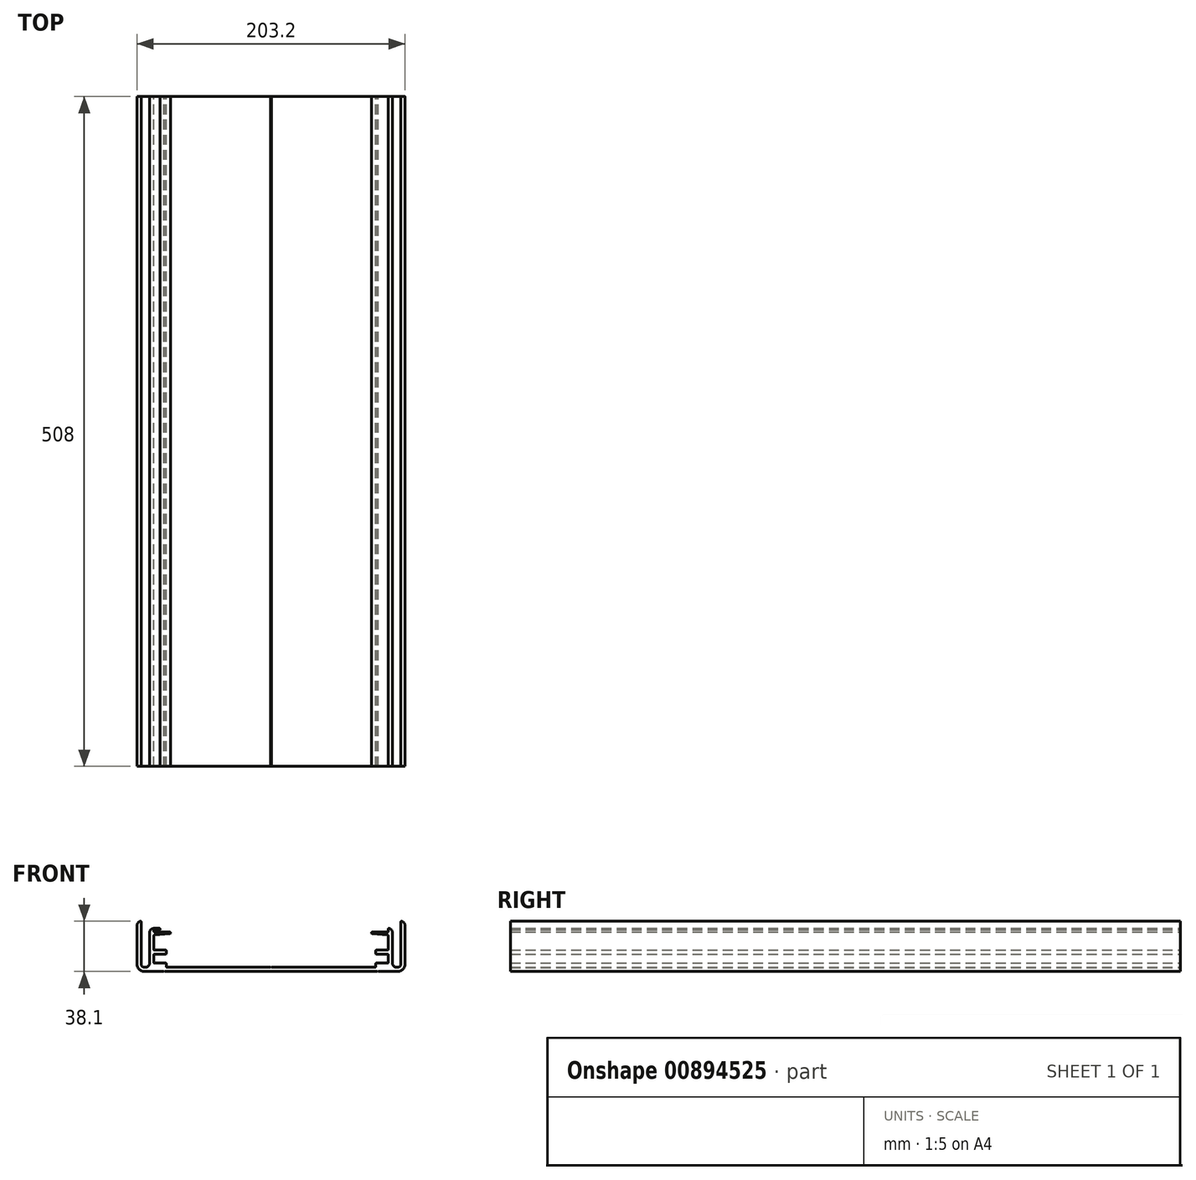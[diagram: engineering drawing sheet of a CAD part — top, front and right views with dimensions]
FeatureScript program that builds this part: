
annotation { "Feature Type Name" : "Feature", "Feature Type Description" : "" }
export const myFeature = defineFeature(function(context is Context, id is Id, definition is map)
    precondition{}
    {
        {
            var Q0;
            Q0=qCreatedBy(makeId("Front.planeOp"),FACE);
            var sketch = newSketch(context, id + "F0", { "sketchPlane" : qUnion([Q0])});
            skLineSegment(sketch, "E0", {"start": v(-109.94, 32.02) * mm, "end": v(-93.65, 25.02) * mm});
            skLineSegment(sketch, "E1", {"start": v(-93.65, 25.02) * mm, "end": v(-89.08, 25.02) * mm});
            skLineSegment(sketch, "E2", {"start": v(-106.68, 29.78) * mm, "end": v(-106.07, 31.2) * mm});
            skLineSegment(sketch, "E3", {"start": v(-106.07, 31.2) * mm, "end": v(-109.94, 32.02) * mm});
            skLineSegment(sketch, "E4", {"start": v(-109.94, 32.02) * mm, "end": v(-106.68, 29.78) * mm});
            skLineSegment(sketch, "E5", {"start": v(-110.7, 32.42) * mm, "end": v(-110.33, 32.8) * mm});
            skLineSegment(sketch, "E6", {"start": v(-109.95, 32.42) * mm, "end": v(-110.33, 32.8) * mm});
            skLineSegment(sketch, "E7", {"start": v(51.95, 32.42) * mm, "end": v(51.57, 32.8) * mm});
            skLineSegment(sketch, "E8", {"start": v(51.19, 32.42) * mm, "end": v(51.57, 32.8) * mm});
            skLineSegment(sketch, "E9", {"start": v(-113.5, 66.15) * mm, "end": v(-113.5, 74.73) * mm});
            skArc(sketch, "E10", {"start": v(49.62, 35.6) * mm, "mid": v(49.88, 35.7) * mm, "end": v(50, 35.97) * mm});
            skArc(sketch, "E11", {"start": v(-108.75, 35.97) * mm, "mid": v(-108.64, 35.7) * mm, "end": v(-108.37, 35.6) * mm});
            skLineSegment(sketch, "E12", {"start": v(-108.37, 35.6) * mm, "end": v(-29.63, 35.6) * mm});
            skLineSegment(sketch, "E13", {"start": v(-29.12, 35.6) * mm, "end": v(49.62, 35.6) * mm});
            skLineSegment(sketch, "E14", {"start": v(51.95, 26.45) * mm, "end": v(51.73, 26.65) * mm});
            skLineSegment(sketch, "E15", {"start": v(51.73, 26.65) * mm, "end": v(50.6, 26.65) * mm});
            skLineSegment(sketch, "E16", {"start": v(50.6, 26.65) * mm, "end": v(50.36, 26.45) * mm});
            skLineSegment(sketch, "E17", {"start": v(50.36, 26.45) * mm, "end": v(50.36, 24.54) * mm});
            skLineSegment(sketch, "E18", {"start": v(51.27, 27.09) * mm, "end": v(51.27, 23.9) * mm});
            skLineSegment(sketch, "E19", {"start": v(51.27, 23.9) * mm, "end": v(52.63, 23.9) * mm});
            skLineSegment(sketch, "E20", {"start": v(50.36, 24.54) * mm, "end": v(50.6, 24.33) * mm});
            skLineSegment(sketch, "E21", {"start": v(50.6, 24.33) * mm, "end": v(51.73, 24.33) * mm});
            skLineSegment(sketch, "E22", {"start": v(51.73, 24.33) * mm, "end": v(51.95, 24.54) * mm});
            skLineSegment(sketch, "E23", {"start": v(-109.74, 14.45) * mm, "end": v(-109.97, 14.65) * mm});
            skLineSegment(sketch, "E24", {"start": v(-109.97, 14.65) * mm, "end": v(-111.1, 14.65) * mm});
            skLineSegment(sketch, "E25", {"start": v(-111.1, 14.65) * mm, "end": v(-111.33, 14.45) * mm});
            skLineSegment(sketch, "E26", {"start": v(-111.33, 14.45) * mm, "end": v(-111.33, 12.54) * mm});
            skLineSegment(sketch, "E27", {"start": v(-110.42, 15.09) * mm, "end": v(-110.42, 11.9) * mm});
            skLineSegment(sketch, "E28", {"start": v(-110.42, 11.9) * mm, "end": v(-109.07, 11.9) * mm});
            skLineSegment(sketch, "E29", {"start": v(-111.33, 12.54) * mm, "end": v(-111.1, 12.33) * mm});
            skLineSegment(sketch, "E30", {"start": v(-111.1, 12.33) * mm, "end": v(-109.97, 12.33) * mm});
            skLineSegment(sketch, "E31", {"start": v(-109.97, 12.33) * mm, "end": v(-109.74, 12.54) * mm});
            skLineSegment(sketch, "E32", {"start": v(51.95, 32.42) * mm, "end": v(66.68, 32.42) * mm});
            skLineSegment(sketch, "E33", {"start": v(-109.95, 32.42) * mm, "end": v(51.19, 32.42) * mm});
            skLineSegment(sketch, "E34", {"start": v(-118.28, 31.04) * mm, "end": v(-118.28, 16.63) * mm});
            skArc(sketch, "E35", {"start": v(-108.75, 38.39) * mm, "mid": v(-108.87, 38.66) * mm, "end": v(-109.13, 38.77) * mm});
            skLineSegment(sketch, "E36", {"start": v(-125.44, 32.42) * mm, "end": v(-110.7, 32.42) * mm});
            skLineSegment(sketch, "E37", {"start": v(-110.33, 35.85) * mm, "end": v(-110.33, 11.74) * mm});
            skLineSegment(sketch, "E38", {"start": v(92.16, -20.96) * mm, "end": v(91.21, -19.68) * mm});
            skLineSegment(sketch, "E39", {"start": v(91.21, -17.46) * mm, "end": v(92.16, -16.19) * mm});
            skLineSegment(sketch, "E40", {"start": v(93.8, -20.16) * mm, "end": v(94.65, -18.04) * mm});
            skLineSegment(sketch, "E41", {"start": v(94.65, -18.04) * mm, "end": v(95.5, -20.16) * mm});
            skLineSegment(sketch, "E42", {"start": v(95.5, -20.16) * mm, "end": v(93.8, -20.16) * mm});
            skLineSegment(sketch, "E43", {"start": v(97.56, -20.96) * mm, "end": v(98.51, -19.68) * mm});
            skLineSegment(sketch, "E44", {"start": v(98.51, -19.68) * mm, "end": v(98.51, -17.46) * mm});
            skLineSegment(sketch, "E45", {"start": v(98.51, -17.46) * mm, "end": v(97.56, -16.19) * mm});
            skLineSegment(sketch, "E46", {"start": v(101.07, -20.16) * mm, "end": v(101.29, -20.16) * mm});
            skLineSegment(sketch, "E47", {"start": v(101.29, -20.16) * mm, "end": v(101.29, -19.95) * mm});
            skLineSegment(sketch, "E48", {"start": v(101.29, -19.95) * mm, "end": v(101.07, -19.95) * mm});
            skLineSegment(sketch, "E49", {"start": v(101.07, -19.95) * mm, "end": v(101.07, -20.16) * mm});
            skLineSegment(sketch, "E50", {"start": v(105.6, -17.84) * mm, "end": v(105.6, -19.32) * mm});
            skLineSegment(sketch, "E51", {"start": v(105.6, -19.32) * mm, "end": v(104.92, -20.16) * mm});
            skLineSegment(sketch, "E52", {"start": v(104.92, -20.16) * mm, "end": v(104.01, -20.16) * mm});
            skLineSegment(sketch, "E53", {"start": v(104.01, -20.16) * mm, "end": v(103.33, -19.32) * mm});
            skLineSegment(sketch, "E54", {"start": v(103.33, -19.32) * mm, "end": v(103.33, -17.84) * mm});
            skLineSegment(sketch, "E55", {"start": v(103.33, -17.84) * mm, "end": v(104.01, -16.98) * mm});
            skLineSegment(sketch, "E56", {"start": v(104.01, -16.98) * mm, "end": v(104.92, -16.98) * mm});
            skLineSegment(sketch, "E57", {"start": v(104.92, -16.98) * mm, "end": v(105.6, -17.84) * mm});
            skLineSegment(sketch, "E58", {"start": v(108.77, -18.25) * mm, "end": v(108.1, -18.89) * mm});
            skLineSegment(sketch, "E59", {"start": v(108.77, -20.16) * mm, "end": v(106.5, -20.16) * mm});
            skLineSegment(sketch, "E60", {"start": v(106.5, -20.16) * mm, "end": v(106.5, -19.74) * mm});
            skLineSegment(sketch, "E61", {"start": v(106.5, -19.74) * mm, "end": v(107.19, -19.1) * mm});
            skLineSegment(sketch, "E62", {"start": v(107.19, -19.1) * mm, "end": v(108.1, -18.89) * mm});
            skLineSegment(sketch, "E63", {"start": v(106.5, -17.62) * mm, "end": v(107.19, -16.98) * mm});
            skLineSegment(sketch, "E64", {"start": v(107.19, -16.98) * mm, "end": v(108.1, -16.98) * mm});
            skLineSegment(sketch, "E65", {"start": v(108.1, -16.98) * mm, "end": v(108.77, -17.62) * mm});
            skLineSegment(sketch, "E66", {"start": v(108.77, -17.62) * mm, "end": v(108.77, -18.25) * mm});
            skLineSegment(sketch, "E67", {"start": v(111.5, -18.47) * mm, "end": v(111.95, -18.89) * mm});
            skLineSegment(sketch, "E68", {"start": v(110.6, -18.47) * mm, "end": v(111.5, -18.47) * mm});
            skLineSegment(sketch, "E69", {"start": v(111.5, -18.47) * mm, "end": v(111.95, -18.04) * mm});
            skLineSegment(sketch, "E70", {"start": v(111.95, -18.89) * mm, "end": v(111.95, -19.74) * mm});
            skLineSegment(sketch, "E71", {"start": v(111.95, -19.74) * mm, "end": v(111.5, -20.16) * mm});
            skLineSegment(sketch, "E72", {"start": v(111.5, -20.16) * mm, "end": v(109.9, -20.16) * mm});
            skLineSegment(sketch, "E73", {"start": v(109.9, -20.16) * mm, "end": v(109.68, -19.95) * mm});
            skLineSegment(sketch, "E74", {"start": v(109.9, -17.2) * mm, "end": v(110.14, -16.98) * mm});
            skLineSegment(sketch, "E75", {"start": v(110.14, -16.98) * mm, "end": v(111.5, -16.98) * mm});
            skLineSegment(sketch, "E76", {"start": v(111.5, -16.98) * mm, "end": v(111.95, -17.42) * mm});
            skLineSegment(sketch, "E77", {"start": v(111.95, -17.42) * mm, "end": v(111.95, -18.04) * mm});
            skLineSegment(sketch, "E78", {"start": v(118.3, -18.25) * mm, "end": v(117.85, -18.68) * mm});
            skLineSegment(sketch, "E79", {"start": v(117.85, -18.68) * mm, "end": v(116.03, -18.68) * mm});
            skLineSegment(sketch, "E80", {"start": v(116.03, -20.16) * mm, "end": v(116.03, -16.98) * mm});
            skLineSegment(sketch, "E81", {"start": v(116.03, -16.98) * mm, "end": v(117.85, -16.98) * mm});
            skLineSegment(sketch, "E82", {"start": v(117.85, -16.98) * mm, "end": v(118.3, -17.42) * mm});
            skLineSegment(sketch, "E83", {"start": v(118.3, -17.42) * mm, "end": v(118.3, -18.25) * mm});
            skLineSegment(sketch, "E84", {"start": v(117.4, -18.68) * mm, "end": v(118.3, -20.16) * mm});
            skLineSegment(sketch, "E85", {"start": v(120.12, -20.16) * mm, "end": v(120.34, -20.16) * mm});
            skLineSegment(sketch, "E86", {"start": v(120.34, -20.16) * mm, "end": v(120.34, -19.95) * mm});
            skLineSegment(sketch, "E87", {"start": v(120.34, -19.95) * mm, "end": v(120.12, -19.95) * mm});
            skLineSegment(sketch, "E88", {"start": v(120.12, -19.95) * mm, "end": v(120.12, -20.16) * mm});
            skLineSegment(sketch, "E89", {"start": v(123.91, -20.96) * mm, "end": v(122.96, -19.68) * mm});
            skLineSegment(sketch, "E90", {"start": v(122.96, -19.68) * mm, "end": v(122.96, -17.46) * mm});
            skLineSegment(sketch, "E91", {"start": v(122.96, -17.46) * mm, "end": v(123.91, -16.19) * mm});
            skLineSegment(sketch, "E92", {"start": v(126.24, -20.16) * mm, "end": v(127.15, -20.16) * mm});
            skLineSegment(sketch, "E93", {"start": v(126.24, -17.42) * mm, "end": v(126.69, -16.98) * mm});
            skLineSegment(sketch, "E94", {"start": v(129.41, -20.16) * mm, "end": v(130.32, -20.16) * mm});
            skLineSegment(sketch, "E95", {"start": v(129.41, -17.42) * mm, "end": v(129.86, -16.98) * mm});
            skLineSegment(sketch, "E96", {"start": v(129.86, -16.98) * mm, "end": v(129.86, -20.16) * mm});
            skLineSegment(sketch, "E97", {"start": v(132.49, -20.96) * mm, "end": v(133.44, -19.68) * mm});
            skLineSegment(sketch, "E98", {"start": v(133.44, -19.68) * mm, "end": v(133.44, -17.46) * mm});
            skLineSegment(sketch, "E99", {"start": v(133.44, -17.46) * mm, "end": v(132.49, -16.19) * mm});
            skLineSegment(sketch, "E100", {"start": v(66.98, 70.95) * mm, "end": v(67.65, 72.64) * mm});
            skLineSegment(sketch, "E101", {"start": v(67.65, 72.64) * mm, "end": v(68.33, 70.95) * mm});
            skLineSegment(sketch, "E102", {"start": v(68.33, 70.95) * mm, "end": v(66.98, 70.95) * mm});
            skLineSegment(sketch, "E103", {"start": v(-127, 70.86) * mm, "end": v(-126.33, 72.55) * mm});
            skLineSegment(sketch, "E104", {"start": v(-126.33, 72.55) * mm, "end": v(-125.65, 70.86) * mm});
            skLineSegment(sketch, "E105", {"start": v(-125.65, 70.86) * mm, "end": v(-127, 70.86) * mm});
            skLineSegment(sketch, "E106", {"start": v(-118.28, 37.9) * mm, "end": v(-118.28, 33.4) * mm});
            skArc(sketch, "E107", {"start": v(-128.52, 70.5) * mm, "mid": v(-130.29, 69.39) * mm, "end": v(-130.98, 67.41) * mm});
            skArc(sketch, "E108", {"start": v(-127.8, 69.93) * mm, "mid": v(-128.02, 70.4) * mm, "end": v(-128.52, 70.5) * mm});
            skArc(sketch, "E109", {"start": v(-127.8, 37.96) * mm, "mid": v(-127.11, 36.29) * mm, "end": v(-125.44, 35.6) * mm});
            skArc(sketch, "E110", {"start": v(-130.98, 37.96) * mm, "mid": v(-129.36, 34.04) * mm, "end": v(-125.44, 32.42) * mm});
            skArc(sketch, "E111", {"start": v(-124.63, 35.6) * mm, "mid": v(-122.38, 36.52) * mm, "end": v(-121.45, 38.77) * mm});
            skLineSegment(sketch, "E112", {"start": v(-125.44, 35.6) * mm, "end": v(-124.63, 35.6) * mm});
            skLineSegment(sketch, "E113", {"start": v(-130.98, 37.96) * mm, "end": v(-130.98, 67.41) * mm});
            skLineSegment(sketch, "E114", {"start": v(-127.8, 37.96) * mm, "end": v(-127.8, 69.93) * mm});
            skLineSegment(sketch, "E115", {"start": v(-108.75, 38.39) * mm, "end": v(-108.75, 35.97) * mm});
            skArc(sketch, "E116", {"start": v(72.22, 67.41) * mm, "mid": v(71.53, 69.39) * mm, "end": v(69.76, 70.5) * mm});
            skArc(sketch, "E117", {"start": v(50.38, 38.77) * mm, "mid": v(50.1, 38.66) * mm, "end": v(50, 38.39) * mm});
            skArc(sketch, "E118", {"start": v(59.14, 38.77) * mm, "mid": v(59.4, 38.88) * mm, "end": v(59.52, 39.15) * mm});
            skArc(sketch, "E119", {"start": v(62.7, 38.77) * mm, "mid": v(63.63, 36.52) * mm, "end": v(65.87, 35.6) * mm});
            skArc(sketch, "E120", {"start": v(66.68, 35.6) * mm, "mid": v(68.35, 36.29) * mm, "end": v(69.05, 37.96) * mm});
            skArc(sketch, "E121", {"start": v(66.68, 32.42) * mm, "mid": v(70.6, 34.04) * mm, "end": v(72.22, 37.96) * mm});
            skLineSegment(sketch, "E122", {"start": v(65.87, 35.6) * mm, "end": v(66.68, 35.6) * mm});
            skArc(sketch, "E123", {"start": v(69.76, 70.5) * mm, "mid": v(69.27, 70.4) * mm, "end": v(69.05, 69.93) * mm});
            skLineSegment(sketch, "E124", {"start": v(50, 35.97) * mm, "end": v(50, 38.39) * mm});
            skLineSegment(sketch, "E125", {"start": v(50.38, 38.77) * mm, "end": v(59.14, 38.77) * mm});
            skLineSegment(sketch, "E126", {"start": v(72.22, 37.96) * mm, "end": v(72.22, 67.41) * mm});
            skLineSegment(sketch, "E127", {"start": v(69.05, 37.96) * mm, "end": v(69.05, 69.93) * mm});
            skLineSegment(sketch, "E128", {"start": v(-29.63, 35.6) * mm, "end": v(-29.38, 35.34) * mm});
            skLineSegment(sketch, "E129", {"start": v(-29.12, 35.6) * mm, "end": v(-29.38, 35.34) * mm});
            skLineSegment(sketch, "E130", {"start": v(-30.82, 45.5) * mm, "end": v(-30.82, 44.28) * mm});
            skLineSegment(sketch, "E131", {"start": v(-30.82, 44.28) * mm, "end": v(-29.97, 43.42) * mm});
            skLineSegment(sketch, "E132", {"start": v(-29.97, 43.42) * mm, "end": v(-28.75, 43.42) * mm});
            skLineSegment(sketch, "E133", {"start": v(-28.75, 43.42) * mm, "end": v(-27.88, 44.28) * mm});
            skLineSegment(sketch, "E134", {"start": v(-27.88, 44.28) * mm, "end": v(-27.88, 45.5) * mm});
            skLineSegment(sketch, "E135", {"start": v(-27.88, 45.5) * mm, "end": v(-28.75, 46.36) * mm});
            skLineSegment(sketch, "E136", {"start": v(-28.75, 46.36) * mm, "end": v(-29.97, 46.36) * mm});
            skLineSegment(sketch, "E137", {"start": v(-29.97, 46.36) * mm, "end": v(-30.82, 45.5) * mm});
            skLineSegment(sketch, "E138", {"start": v(-31.55, 45.8) * mm, "end": v(-31.55, 43.97) * mm});
            skLineSegment(sketch, "E139", {"start": v(-31.55, 43.97) * mm, "end": v(-30.26, 42.68) * mm});
            skLineSegment(sketch, "E140", {"start": v(-30.26, 42.68) * mm, "end": v(-28.44, 42.68) * mm});
            skLineSegment(sketch, "E141", {"start": v(-28.44, 42.68) * mm, "end": v(-27.16, 43.97) * mm});
            skLineSegment(sketch, "E142", {"start": v(-27.16, 43.97) * mm, "end": v(-27.16, 45.8) * mm});
            skLineSegment(sketch, "E143", {"start": v(-27.16, 45.8) * mm, "end": v(-28.44, 47.1) * mm});
            skLineSegment(sketch, "E144", {"start": v(-28.44, 47.1) * mm, "end": v(-30.26, 47.1) * mm});
            skLineSegment(sketch, "E145", {"start": v(-30.26, 47.1) * mm, "end": v(-31.55, 45.8) * mm});
            skLineSegment(sketch, "E146", {"start": v(-28.86, 40.34) * mm, "end": v(-29.9, 40.34) * mm});
            skLineSegment(sketch, "E147", {"start": v(-113.25, 63.86) * mm, "end": v(-106.42, 63.86) * mm});
            skLineSegment(sketch, "E148", {"start": v(-105.58, 75.44) * mm, "end": v(-105.58, 86.36) * mm});
            skLineSegment(sketch, "E149", {"start": v(-105.58, 62.26) * mm, "end": v(-105.58, 72.73) * mm});
            skLineSegment(sketch, "E150", {"start": v(57.68, 65.46) * mm, "end": v(58.36, 67.15) * mm});
            skLineSegment(sketch, "E151", {"start": v(58.36, 67.15) * mm, "end": v(59.03, 65.46) * mm});
            skLineSegment(sketch, "E152", {"start": v(59.03, 65.46) * mm, "end": v(57.68, 65.46) * mm});
            skLineSegment(sketch, "E153", {"start": v(45, 62.94) * mm, "end": v(45.68, 64.64) * mm});
            skLineSegment(sketch, "E154", {"start": v(45.68, 64.64) * mm, "end": v(46.35, 62.94) * mm});
            skLineSegment(sketch, "E155", {"start": v(46.35, 62.94) * mm, "end": v(45, 62.94) * mm});
            skLineSegment(sketch, "E156", {"start": v(47.9, 48.79) * mm, "end": v(48.57, 50.48) * mm});
            skLineSegment(sketch, "E157", {"start": v(48.57, 50.48) * mm, "end": v(49.24, 48.79) * mm});
            skLineSegment(sketch, "E158", {"start": v(49.24, 48.79) * mm, "end": v(47.9, 48.79) * mm});
            skLineSegment(sketch, "E159", {"start": v(48.08, 43.57) * mm, "end": v(48.75, 45.26) * mm});
            skLineSegment(sketch, "E160", {"start": v(48.75, 45.26) * mm, "end": v(49.43, 43.57) * mm});
            skLineSegment(sketch, "E161", {"start": v(49.43, 43.57) * mm, "end": v(48.08, 43.57) * mm});
            skLineSegment(sketch, "E162", {"start": v(57.3, 57.72) * mm, "end": v(57.98, 59.42) * mm});
            skLineSegment(sketch, "E163", {"start": v(57.98, 59.42) * mm, "end": v(58.66, 57.72) * mm});
            skLineSegment(sketch, "E164", {"start": v(58.66, 57.72) * mm, "end": v(57.3, 57.72) * mm});
            skLineSegment(sketch, "E165", {"start": v(-117.42, 57.63) * mm, "end": v(-116.75, 59.32) * mm});
            skLineSegment(sketch, "E166", {"start": v(-116.75, 59.32) * mm, "end": v(-116.07, 57.63) * mm});
            skLineSegment(sketch, "E167", {"start": v(-116.07, 57.63) * mm, "end": v(-117.42, 57.63) * mm});
            skLineSegment(sketch, "E168", {"start": v(-108.2, 49.35) * mm, "end": v(-107.52, 51.04) * mm});
            skLineSegment(sketch, "E169", {"start": v(-107.52, 51.04) * mm, "end": v(-106.84, 49.35) * mm});
            skLineSegment(sketch, "E170", {"start": v(-106.84, 49.35) * mm, "end": v(-108.2, 49.35) * mm});
            skLineSegment(sketch, "E171", {"start": v(-107.91, 43) * mm, "end": v(-107.24, 44.7) * mm});
            skLineSegment(sketch, "E172", {"start": v(-107.24, 44.7) * mm, "end": v(-106.56, 43) * mm});
            skLineSegment(sketch, "E173", {"start": v(-106.56, 43) * mm, "end": v(-107.91, 43) * mm});
            skLineSegment(sketch, "E174", {"start": v(-105.21, 59.96) * mm, "end": v(-104.54, 61.65) * mm});
            skLineSegment(sketch, "E175", {"start": v(-104.54, 61.65) * mm, "end": v(-103.86, 59.96) * mm});
            skLineSegment(sketch, "E176", {"start": v(-103.86, 59.96) * mm, "end": v(-105.21, 59.96) * mm});
            skArc(sketch, "E177", {"start": v(150.69, 128.9) * mm, "mid": v(149.97, 128.6) * mm, "end": v(149.67, 127.89) * mm});
            skArc(sketch, "E178", {"start": v(149.67, 113.41) * mm, "mid": v(149.97, 112.7) * mm, "end": v(150.69, 112.4) * mm});
            skArc(sketch, "E179", {"start": v(203.26, 112.4) * mm, "mid": v(203.98, 112.7) * mm, "end": v(204.28, 113.41) * mm});
            skArc(sketch, "E180", {"start": v(204.28, 127.89) * mm, "mid": v(203.98, 128.6) * mm, "end": v(203.26, 128.9) * mm});
            skArc(sketch, "E181", {"start": v(122.43, -114.05) * mm, "mid": v(122.52, -114.16) * mm, "end": v(122.66, -114.2) * mm});
            skArc(sketch, "E182", {"start": v(122.3, -112.39) * mm, "mid": v(122.12, -112.47) * mm, "end": v(122.06, -112.67) * mm});
            skArc(sketch, "E183", {"start": v(122.06, -110.84) * mm, "mid": v(122.12, -111.04) * mm, "end": v(122.3, -111.12) * mm});
            skArc(sketch, "E184", {"start": v(122.66, -109.31) * mm, "mid": v(122.52, -109.35) * mm, "end": v(122.43, -109.46) * mm});
            skArc(sketch, "E185", {"start": v(122.06, -112.67) * mm, "mid": v(122.2, -113.37) * mm, "end": v(122.43, -114.05) * mm});
            skArc(sketch, "E186", {"start": v(121.33, -114.7) * mm, "mid": v(121.8, -115.26) * mm, "end": v(122.5, -115.47) * mm});
            skArc(sketch, "E187", {"start": v(122.5, -108.04) * mm, "mid": v(121.8, -108.25) * mm, "end": v(121.33, -108.8) * mm});
            skArc(sketch, "E188", {"start": v(122.43, -109.46) * mm, "mid": v(122.2, -110.14) * mm, "end": v(122.06, -110.84) * mm});
            skArc(sketch, "E189", {"start": v(121.33, -108.8) * mm, "mid": v(120.72, -111.76) * mm, "end": v(121.33, -114.7) * mm});
            skArc(sketch, "E190", {"start": v(142.26, -114.2) * mm, "mid": v(142.4, -114.15) * mm, "end": v(142.5, -114.04) * mm});
            skArc(sketch, "E191", {"start": v(141.11, -114.04) * mm, "mid": v(141.2, -114.15) * mm, "end": v(141.34, -114.2) * mm});
            skArc(sketch, "E192", {"start": v(142.5, -110.96) * mm, "mid": v(142.4, -110.84) * mm, "end": v(142.26, -110.8) * mm});
            skArc(sketch, "E193", {"start": v(141.34, -110.8) * mm, "mid": v(141.2, -110.84) * mm, "end": v(141.11, -110.96) * mm});
            skArc(sketch, "E194", {"start": v(141.11, -110.96) * mm, "mid": v(140.85, -112.5) * mm, "end": v(141.11, -114.04) * mm});
            skArc(sketch, "E195", {"start": v(142.5, -114.04) * mm, "mid": v(142.75, -112.5) * mm, "end": v(142.5, -110.96) * mm});
            skArc(sketch, "E196", {"start": v(137.15, -114.04) * mm, "mid": v(137.24, -114.15) * mm, "end": v(137.38, -114.2) * mm});
            skArc(sketch, "E197", {"start": v(137.38, -110.8) * mm, "mid": v(137.24, -110.84) * mm, "end": v(137.15, -110.96) * mm});
            skArc(sketch, "E198", {"start": v(136.03, -114.66) * mm, "mid": v(136.5, -115.25) * mm, "end": v(137.21, -115.47) * mm});
            skArc(sketch, "E199", {"start": v(137.21, -109.52) * mm, "mid": v(136.5, -109.75) * mm, "end": v(136.03, -110.33) * mm});
            skArc(sketch, "E200", {"start": v(140, -114.66) * mm, "mid": v(140.46, -115.25) * mm, "end": v(141.17, -115.47) * mm});
            skArc(sketch, "E201", {"start": v(142.43, -115.47) * mm, "mid": v(143.15, -115.25) * mm, "end": v(143.61, -114.66) * mm});
            skArc(sketch, "E202", {"start": v(143.61, -110.33) * mm, "mid": v(143.15, -109.75) * mm, "end": v(142.43, -109.52) * mm});
            skArc(sketch, "E203", {"start": v(141.17, -109.52) * mm, "mid": v(140.46, -109.75) * mm, "end": v(140, -110.33) * mm});
            skArc(sketch, "E204", {"start": v(143.61, -114.66) * mm, "mid": v(144.02, -112.5) * mm, "end": v(143.61, -110.33) * mm});
            skArc(sketch, "E205", {"start": v(137.15, -110.96) * mm, "mid": v(136.89, -112.5) * mm, "end": v(137.15, -114.04) * mm});
            skArc(sketch, "E206", {"start": v(136.03, -110.33) * mm, "mid": v(135.62, -112.5) * mm, "end": v(136.03, -114.66) * mm});
            skArc(sketch, "E207", {"start": v(140, -110.33) * mm, "mid": v(139.58, -112.5) * mm, "end": v(140, -114.66) * mm});
            skArc(sketch, "E208", {"start": v(125.23, -115.47) * mm, "mid": v(125.4, -115.4) * mm, "end": v(125.48, -115.22) * mm});
            skArc(sketch, "E209", {"start": v(125.48, -114.45) * mm, "mid": v(125.4, -114.27) * mm, "end": v(125.23, -114.2) * mm});
            skArc(sketch, "E210", {"start": v(125.23, -112.39) * mm, "mid": v(125.4, -112.32) * mm, "end": v(125.48, -112.14) * mm});
            skArc(sketch, "E211", {"start": v(125.48, -111.37) * mm, "mid": v(125.4, -111.2) * mm, "end": v(125.23, -111.12) * mm});
            skArc(sketch, "E212", {"start": v(125.48, -108.29) * mm, "mid": v(125.4, -108.11) * mm, "end": v(125.23, -108.04) * mm});
            skArc(sketch, "E213", {"start": v(125.23, -109.31) * mm, "mid": v(125.4, -109.24) * mm, "end": v(125.48, -109.07) * mm});
            skArc(sketch, "E214", {"start": v(139.02, -115.47) * mm, "mid": v(139.2, -115.4) * mm, "end": v(139.27, -115.22) * mm});
            skArc(sketch, "E215", {"start": v(139.27, -114.45) * mm, "mid": v(139.2, -114.27) * mm, "end": v(139.02, -114.2) * mm});
            skArc(sketch, "E216", {"start": v(139.02, -110.8) * mm, "mid": v(139.2, -110.72) * mm, "end": v(139.27, -110.55) * mm});
            skArc(sketch, "E217", {"start": v(139.27, -109.77) * mm, "mid": v(139.2, -109.6) * mm, "end": v(139.02, -109.52) * mm});
            skArc(sketch, "E218", {"start": v(149.93, -109.51) * mm, "mid": v(149.84, -109.37) * mm, "end": v(149.68, -109.31) * mm});
            skArc(sketch, "E219", {"start": v(149.14, -109.31) * mm, "mid": v(148.98, -109.37) * mm, "end": v(148.9, -109.51) * mm});
            skArc(sketch, "E220", {"start": v(150.11, -112.22) * mm, "mid": v(150.3, -112.13) * mm, "end": v(150.35, -111.93) * mm});
            skArc(sketch, "E221", {"start": v(148.47, -111.93) * mm, "mid": v(148.52, -112.13) * mm, "end": v(148.71, -112.22) * mm});
            skArc(sketch, "E222", {"start": v(151.97, -115.47) * mm, "mid": v(152.16, -115.38) * mm, "end": v(152.21, -115.18) * mm});
            skArc(sketch, "E223", {"start": v(150.94, -115.27) * mm, "mid": v(151.02, -115.41) * mm, "end": v(151.18, -115.47) * mm});
            skArc(sketch, "E224", {"start": v(150.66, -113.7) * mm, "mid": v(150.58, -113.54) * mm, "end": v(150.42, -113.49) * mm});
            skArc(sketch, "E225", {"start": v(148.4, -113.49) * mm, "mid": v(148.24, -113.54) * mm, "end": v(148.16, -113.7) * mm});
            skArc(sketch, "E226", {"start": v(147.64, -115.47) * mm, "mid": v(147.8, -115.41) * mm, "end": v(147.88, -115.27) * mm});
            skArc(sketch, "E227", {"start": v(146.6, -115.18) * mm, "mid": v(146.66, -115.38) * mm, "end": v(146.85, -115.47) * mm});
            skArc(sketch, "E228", {"start": v(151, -108.25) * mm, "mid": v(150.9, -108.1) * mm, "end": v(150.75, -108.04) * mm});
            skArc(sketch, "E229", {"start": v(148.07, -108.04) * mm, "mid": v(147.92, -108.1) * mm, "end": v(147.83, -108.25) * mm});
            skArc(sketch, "E230", {"start": v(154, -108.29) * mm, "mid": v(153.94, -108.11) * mm, "end": v(153.76, -108.04) * mm});
            skArc(sketch, "E231", {"start": v(152.99, -108.04) * mm, "mid": v(152.81, -108.11) * mm, "end": v(152.74, -108.29) * mm});
            skArc(sketch, "E232", {"start": v(153.76, -115.47) * mm, "mid": v(153.94, -115.4) * mm, "end": v(154, -115.22) * mm});
            skArc(sketch, "E233", {"start": v(152.74, -115.22) * mm, "mid": v(152.81, -115.4) * mm, "end": v(152.99, -115.47) * mm});
            skArc(sketch, "E234", {"start": v(157.65, -115.15) * mm, "mid": v(157.53, -114.94) * mm, "end": v(157.28, -114.94) * mm});
            skArc(sketch, "E235", {"start": v(158.68, -115.47) * mm, "mid": v(158.85, -115.4) * mm, "end": v(158.92, -115.22) * mm});
            skArc(sketch, "E236", {"start": v(157.65, -115.22) * mm, "mid": v(157.72, -115.4) * mm, "end": v(157.9, -115.47) * mm});
            skArc(sketch, "E237", {"start": v(154.73, -109.52) * mm, "mid": v(154.56, -109.6) * mm, "end": v(154.48, -109.77) * mm});
            skArc(sketch, "E238", {"start": v(155.75, -109.77) * mm, "mid": v(155.68, -109.6) * mm, "end": v(155.5, -109.52) * mm});
            skArc(sketch, "E239", {"start": v(158.92, -109.77) * mm, "mid": v(158.85, -109.6) * mm, "end": v(158.68, -109.52) * mm});
            skArc(sketch, "E240", {"start": v(157.9, -109.52) * mm, "mid": v(157.72, -109.6) * mm, "end": v(157.65, -109.77) * mm});
            skArc(sketch, "E241", {"start": v(168.5, -108.68) * mm, "mid": v(168.68, -108.6) * mm, "end": v(168.75, -108.43) * mm});
            skArc(sketch, "E242", {"start": v(168.75, -108.29) * mm, "mid": v(168.68, -108.11) * mm, "end": v(168.5, -108.04) * mm});
            skArc(sketch, "E243", {"start": v(167.48, -108.43) * mm, "mid": v(167.55, -108.6) * mm, "end": v(167.73, -108.68) * mm});
            skArc(sketch, "E244", {"start": v(168.75, -109.77) * mm, "mid": v(168.68, -109.6) * mm, "end": v(168.5, -109.52) * mm});
            skArc(sketch, "E245", {"start": v(167.73, -109.52) * mm, "mid": v(167.55, -109.6) * mm, "end": v(167.48, -109.77) * mm});
            skArc(sketch, "E246", {"start": v(168.5, -115.47) * mm, "mid": v(168.68, -115.4) * mm, "end": v(168.75, -115.22) * mm});
            skArc(sketch, "E247", {"start": v(167.48, -115.22) * mm, "mid": v(167.55, -115.4) * mm, "end": v(167.73, -115.47) * mm});
            skArc(sketch, "E248", {"start": v(166.76, -115.47) * mm, "mid": v(166.93, -115.4) * mm, "end": v(167, -115.22) * mm});
            skArc(sketch, "E249", {"start": v(165.74, -115.22) * mm, "mid": v(165.8, -115.4) * mm, "end": v(165.98, -115.47) * mm});
            skArc(sketch, "E250", {"start": v(163.59, -115.47) * mm, "mid": v(163.76, -115.4) * mm, "end": v(163.83, -115.22) * mm});
            skArc(sketch, "E251", {"start": v(162.57, -115.22) * mm, "mid": v(162.64, -115.4) * mm, "end": v(162.81, -115.47) * mm});
            skArc(sketch, "E252", {"start": v(160.42, -115.47) * mm, "mid": v(160.6, -115.4) * mm, "end": v(160.66, -115.22) * mm});
            skArc(sketch, "E253", {"start": v(159.4, -115.22) * mm, "mid": v(159.47, -115.4) * mm, "end": v(159.64, -115.47) * mm});
            skArc(sketch, "E254", {"start": v(163.57, -110.16) * mm, "mid": v(163.71, -110.26) * mm, "end": v(163.89, -110.23) * mm});
            skArc(sketch, "E255", {"start": v(160.66, -109.84) * mm, "mid": v(160.79, -110.05) * mm, "end": v(161.03, -110.05) * mm});
            skArc(sketch, "E256", {"start": v(160.66, -109.77) * mm, "mid": v(160.6, -109.6) * mm, "end": v(160.42, -109.52) * mm});
            skArc(sketch, "E257", {"start": v(159.64, -109.52) * mm, "mid": v(159.47, -109.6) * mm, "end": v(159.4, -109.77) * mm});
            skArc(sketch, "E258", {"start": v(167.73, -108.04) * mm, "mid": v(167.55, -108.11) * mm, "end": v(167.48, -108.29) * mm});
            skArc(sketch, "E259", {"start": v(170.25, -115.47) * mm, "mid": v(170.42, -115.4) * mm, "end": v(170.5, -115.22) * mm});
            skArc(sketch, "E260", {"start": v(169.22, -115.22) * mm, "mid": v(169.3, -115.4) * mm, "end": v(169.47, -115.47) * mm});
            skArc(sketch, "E261", {"start": v(169.47, -109.52) * mm, "mid": v(169.3, -109.6) * mm, "end": v(169.22, -109.77) * mm});
            skArc(sketch, "E262", {"start": v(170.5, -109.84) * mm, "mid": v(170.61, -110.05) * mm, "end": v(170.86, -110.05) * mm});
            skArc(sketch, "E263", {"start": v(170.5, -109.77) * mm, "mid": v(170.42, -109.6) * mm, "end": v(170.25, -109.52) * mm});
            skArc(sketch, "E264", {"start": v(173.42, -115.47) * mm, "mid": v(173.59, -115.4) * mm, "end": v(173.66, -115.22) * mm});
            skArc(sketch, "E265", {"start": v(172.4, -115.22) * mm, "mid": v(172.47, -115.4) * mm, "end": v(172.64, -115.47) * mm});
            skArc(sketch, "E266", {"start": v(178.33, -115.47) * mm, "mid": v(178.5, -115.4) * mm, "end": v(178.57, -115.22) * mm});
            skArc(sketch, "E267", {"start": v(177.3, -115.22) * mm, "mid": v(177.38, -115.4) * mm, "end": v(177.55, -115.47) * mm});
            skArc(sketch, "E268", {"start": v(177.3, -115.15) * mm, "mid": v(177.18, -114.94) * mm, "end": v(176.94, -114.94) * mm});
            skArc(sketch, "E269", {"start": v(178.57, -109.77) * mm, "mid": v(178.5, -109.6) * mm, "end": v(178.33, -109.52) * mm});
            skArc(sketch, "E270", {"start": v(177.55, -109.52) * mm, "mid": v(177.38, -109.6) * mm, "end": v(177.3, -109.77) * mm});
            skArc(sketch, "E271", {"start": v(175.4, -109.77) * mm, "mid": v(175.33, -109.6) * mm, "end": v(175.16, -109.52) * mm});
            skArc(sketch, "E272", {"start": v(174.38, -109.52) * mm, "mid": v(174.2, -109.6) * mm, "end": v(174.14, -109.77) * mm});
            skArc(sketch, "E273", {"start": v(183.22, -110.16) * mm, "mid": v(183.37, -110.26) * mm, "end": v(183.54, -110.23) * mm});
            skArc(sketch, "E274", {"start": v(180.32, -109.84) * mm, "mid": v(180.44, -110.05) * mm, "end": v(180.69, -110.05) * mm});
            skArc(sketch, "E275", {"start": v(180.32, -109.77) * mm, "mid": v(180.25, -109.6) * mm, "end": v(180.07, -109.52) * mm});
            skArc(sketch, "E276", {"start": v(179.3, -109.52) * mm, "mid": v(179.12, -109.6) * mm, "end": v(179.05, -109.77) * mm});
            skArc(sketch, "E277", {"start": v(186.41, -115.47) * mm, "mid": v(186.59, -115.4) * mm, "end": v(186.66, -115.22) * mm});
            skArc(sketch, "E278", {"start": v(183.24, -115.47) * mm, "mid": v(183.42, -115.4) * mm, "end": v(183.49, -115.22) * mm});
            skArc(sketch, "E279", {"start": v(180.07, -115.47) * mm, "mid": v(180.25, -115.4) * mm, "end": v(180.32, -115.22) * mm});
            skArc(sketch, "E280", {"start": v(179.05, -115.22) * mm, "mid": v(179.12, -115.4) * mm, "end": v(179.3, -115.47) * mm});
            skArc(sketch, "E281", {"start": v(182.22, -115.22) * mm, "mid": v(182.3, -115.4) * mm, "end": v(182.47, -115.47) * mm});
            skArc(sketch, "E282", {"start": v(185.39, -115.22) * mm, "mid": v(185.46, -115.4) * mm, "end": v(185.64, -115.47) * mm});
            skArc(sketch, "E283", {"start": v(125.8, -110.55) * mm, "mid": v(125.87, -110.72) * mm, "end": v(126.04, -110.8) * mm});
            skArc(sketch, "E284", {"start": v(126.04, -109.52) * mm, "mid": v(125.87, -109.6) * mm, "end": v(125.8, -109.77) * mm});
            skArc(sketch, "E285", {"start": v(135.15, -109.77) * mm, "mid": v(135.07, -109.6) * mm, "end": v(134.9, -109.52) * mm});
            skArc(sketch, "E286", {"start": v(134.9, -110.8) * mm, "mid": v(135.07, -110.72) * mm, "end": v(135.15, -110.55) * mm});
            skArc(sketch, "E287", {"start": v(130.7, -115.22) * mm, "mid": v(130.78, -115.4) * mm, "end": v(130.95, -115.47) * mm});
            skArc(sketch, "E288", {"start": v(130.95, -114.2) * mm, "mid": v(130.78, -114.27) * mm, "end": v(130.7, -114.45) * mm});
            skArc(sketch, "E289", {"start": v(129.99, -115.47) * mm, "mid": v(130.16, -115.4) * mm, "end": v(130.23, -115.22) * mm});
            skArc(sketch, "E290", {"start": v(127.06, -113.95) * mm, "mid": v(127.14, -114.13) * mm, "end": v(127.3, -114.2) * mm});
            skArc(sketch, "E291", {"start": v(127.3, -113.13) * mm, "mid": v(127.14, -113.2) * mm, "end": v(127.06, -113.38) * mm});
            skArc(sketch, "E292", {"start": v(128.72, -114.2) * mm, "mid": v(128.9, -114.13) * mm, "end": v(128.97, -113.95) * mm});
            skArc(sketch, "E293", {"start": v(128.97, -113.38) * mm, "mid": v(128.9, -113.2) * mm, "end": v(128.72, -113.13) * mm});
            skArc(sketch, "E294", {"start": v(128.72, -111.86) * mm, "mid": v(128.9, -111.8) * mm, "end": v(128.97, -111.62) * mm});
            skArc(sketch, "E295", {"start": v(128.97, -111.04) * mm, "mid": v(128.9, -110.86) * mm, "end": v(128.72, -110.8) * mm});
            skArc(sketch, "E296", {"start": v(125.8, -113.95) * mm, "mid": v(126.24, -115.02) * mm, "end": v(127.3, -115.47) * mm});
            skArc(sketch, "E297", {"start": v(127.3, -111.86) * mm, "mid": v(126.24, -112.3) * mm, "end": v(125.8, -113.38) * mm});
            skArc(sketch, "E298", {"start": v(130.23, -111.04) * mm, "mid": v(129.79, -109.97) * mm, "end": v(128.72, -109.52) * mm});
            skArc(sketch, "E299", {"start": v(130.7, -111.62) * mm, "mid": v(131.15, -112.69) * mm, "end": v(132.22, -113.13) * mm});
            skArc(sketch, "E300", {"start": v(132.22, -109.52) * mm, "mid": v(131.15, -109.97) * mm, "end": v(130.7, -111.04) * mm});
            skArc(sketch, "E301", {"start": v(133.63, -115.47) * mm, "mid": v(134.7, -115.02) * mm, "end": v(135.15, -113.95) * mm});
            skArc(sketch, "E302", {"start": v(135.15, -113.38) * mm, "mid": v(134.7, -112.3) * mm, "end": v(133.63, -111.86) * mm});
            skArc(sketch, "E303", {"start": v(133.63, -114.2) * mm, "mid": v(133.8, -114.13) * mm, "end": v(133.88, -113.95) * mm});
            skArc(sketch, "E304", {"start": v(133.88, -113.38) * mm, "mid": v(133.8, -113.2) * mm, "end": v(133.63, -113.13) * mm});
            skArc(sketch, "E305", {"start": v(131.98, -111.62) * mm, "mid": v(132.05, -111.8) * mm, "end": v(132.22, -111.86) * mm});
            skArc(sketch, "E306", {"start": v(132.22, -110.8) * mm, "mid": v(132.05, -110.86) * mm, "end": v(131.98, -111.04) * mm});
            skArc(sketch, "E307", {"start": v(155.75, -113.46) * mm, "mid": v(155.97, -113.98) * mm, "end": v(156.49, -114.2) * mm});
            skArc(sketch, "E308", {"start": v(156.92, -114.2) * mm, "mid": v(157.44, -113.98) * mm, "end": v(157.65, -113.46) * mm});
            skArc(sketch, "E309", {"start": v(162.57, -111.53) * mm, "mid": v(162.35, -111) * mm, "end": v(161.83, -110.8) * mm});
            skArc(sketch, "E310", {"start": v(161.4, -110.8) * mm, "mid": v(160.88, -111) * mm, "end": v(160.66, -111.53) * mm});
            skArc(sketch, "E311", {"start": v(176.57, -114.2) * mm, "mid": v(177.1, -113.98) * mm, "end": v(177.3, -113.46) * mm});
            skArc(sketch, "E312", {"start": v(175.4, -113.46) * mm, "mid": v(175.62, -113.98) * mm, "end": v(176.14, -114.2) * mm});
            skArc(sketch, "E313", {"start": v(164.57, -110.8) * mm, "mid": v(164.05, -111) * mm, "end": v(163.83, -111.53) * mm});
            skArc(sketch, "E314", {"start": v(165.74, -111.53) * mm, "mid": v(165.52, -111) * mm, "end": v(165, -110.8) * mm});
            skArc(sketch, "E315", {"start": v(171.23, -110.8) * mm, "mid": v(170.7, -111) * mm, "end": v(170.5, -111.53) * mm});
            skArc(sketch, "E316", {"start": v(172.4, -111.53) * mm, "mid": v(172.18, -111) * mm, "end": v(171.66, -110.8) * mm});
            skArc(sketch, "E317", {"start": v(184.22, -110.8) * mm, "mid": v(183.7, -111) * mm, "end": v(183.49, -111.53) * mm});
            skArc(sketch, "E318", {"start": v(181.05, -110.8) * mm, "mid": v(180.53, -111) * mm, "end": v(180.32, -111.53) * mm});
            skArc(sketch, "E319", {"start": v(182.22, -111.53) * mm, "mid": v(182, -111) * mm, "end": v(181.48, -110.8) * mm});
            skArc(sketch, "E320", {"start": v(185.39, -111.53) * mm, "mid": v(185.17, -111) * mm, "end": v(184.65, -110.8) * mm});
            skLineSegment(sketch, "E321", {"start": v(157.65, -113.46) * mm, "end": v(157.65, -109.77) * mm});
            skLineSegment(sketch, "E322", {"start": v(157.65, -115.22) * mm, "end": v(157.65, -115.15) * mm});
            skLineSegment(sketch, "E323", {"start": v(160.66, -109.84) * mm, "end": v(160.66, -109.77) * mm});
            skLineSegment(sketch, "E324", {"start": v(160.66, -115.22) * mm, "end": v(160.66, -111.53) * mm});
            skLineSegment(sketch, "E325", {"start": v(170.5, -109.84) * mm, "end": v(170.5, -109.77) * mm});
            skLineSegment(sketch, "E326", {"start": v(170.5, -115.22) * mm, "end": v(170.5, -111.53) * mm});
            skLineSegment(sketch, "E327", {"start": v(177.3, -113.46) * mm, "end": v(177.3, -109.77) * mm});
            skLineSegment(sketch, "E328", {"start": v(177.3, -115.22) * mm, "end": v(177.3, -115.15) * mm});
            skLineSegment(sketch, "E329", {"start": v(180.32, -109.84) * mm, "end": v(180.32, -109.77) * mm});
            skLineSegment(sketch, "E330", {"start": v(180.32, -115.22) * mm, "end": v(180.32, -111.53) * mm});
            skLineSegment(sketch, "E331", {"start": v(176.37, -115.27) * mm, "end": v(176.94, -114.94) * mm});
            skLineSegment(sketch, "E332", {"start": v(156.72, -115.27) * mm, "end": v(157.28, -114.94) * mm});
            skLineSegment(sketch, "E333", {"start": v(161.03, -110.05) * mm, "end": v(161.6, -109.72) * mm});
            skLineSegment(sketch, "E334", {"start": v(163.89, -110.23) * mm, "end": v(164.77, -109.72) * mm});
            skLineSegment(sketch, "E335", {"start": v(170.86, -110.05) * mm, "end": v(171.43, -109.72) * mm});
            skLineSegment(sketch, "E336", {"start": v(180.69, -110.05) * mm, "end": v(181.25, -109.72) * mm});
            skLineSegment(sketch, "E337", {"start": v(183.54, -110.23) * mm, "end": v(184.42, -109.72) * mm});
            skArc(sketch, "E338", {"start": v(174.14, -113.98) * mm, "mid": v(174.88, -115.27) * mm, "end": v(176.37, -115.27) * mm});
            skArc(sketch, "E339", {"start": v(154.48, -113.98) * mm, "mid": v(155.23, -115.27) * mm, "end": v(156.72, -115.27) * mm});
            skArc(sketch, "E340", {"start": v(183.22, -110.16) * mm, "mid": v(182.32, -109.56) * mm, "end": v(181.25, -109.72) * mm});
            skArc(sketch, "E341", {"start": v(163.57, -110.16) * mm, "mid": v(162.67, -109.56) * mm, "end": v(161.6, -109.72) * mm});
            skArc(sketch, "E342", {"start": v(167, -111.01) * mm, "mid": v(166.26, -109.72) * mm, "end": v(164.77, -109.72) * mm});
            skArc(sketch, "E343", {"start": v(173.66, -111.01) * mm, "mid": v(172.92, -109.72) * mm, "end": v(171.43, -109.72) * mm});
            skArc(sketch, "E344", {"start": v(186.66, -111.01) * mm, "mid": v(185.91, -109.72) * mm, "end": v(184.42, -109.72) * mm});
            skLineSegment(sketch, "E345", {"start": v(151.18, -115.47) * mm, "end": v(151.97, -115.47) * mm});
            skLineSegment(sketch, "E346", {"start": v(146.85, -115.47) * mm, "end": v(147.64, -115.47) * mm});
            skLineSegment(sketch, "E347", {"start": v(150.35, -111.93) * mm, "end": v(149.93, -109.51) * mm});
            skLineSegment(sketch, "E348", {"start": v(150.94, -115.27) * mm, "end": v(150.66, -113.7) * mm});
            skLineSegment(sketch, "E349", {"start": v(148.47, -111.93) * mm, "end": v(148.9, -109.51) * mm});
            skLineSegment(sketch, "E350", {"start": v(147.88, -115.27) * mm, "end": v(148.16, -113.7) * mm});
            skLineSegment(sketch, "E351", {"start": v(148.71, -112.22) * mm, "end": v(150.11, -112.22) * mm});
            skLineSegment(sketch, "E352", {"start": v(148.4, -113.49) * mm, "end": v(150.42, -113.49) * mm});
            skLineSegment(sketch, "E353", {"start": v(152.21, -115.18) * mm, "end": v(151, -108.25) * mm});
            skLineSegment(sketch, "E354", {"start": v(146.6, -115.18) * mm, "end": v(147.83, -108.25) * mm});
            skLineSegment(sketch, "E355", {"start": v(162.81, -115.47) * mm, "end": v(163.59, -115.47) * mm});
            skLineSegment(sketch, "E356", {"start": v(159.64, -115.47) * mm, "end": v(160.42, -115.47) * mm});
            skLineSegment(sketch, "E357", {"start": v(165.98, -115.47) * mm, "end": v(166.76, -115.47) * mm});
            skLineSegment(sketch, "E358", {"start": v(164.57, -110.8) * mm, "end": v(165, -110.8) * mm});
            skLineSegment(sketch, "E359", {"start": v(161.4, -110.8) * mm, "end": v(161.83, -110.8) * mm});
            skLineSegment(sketch, "E360", {"start": v(184.22, -110.8) * mm, "end": v(184.65, -110.8) * mm});
            skLineSegment(sketch, "E361", {"start": v(181.05, -110.8) * mm, "end": v(181.48, -110.8) * mm});
            skLineSegment(sketch, "E362", {"start": v(182.47, -115.47) * mm, "end": v(183.24, -115.47) * mm});
            skLineSegment(sketch, "E363", {"start": v(179.3, -115.47) * mm, "end": v(180.07, -115.47) * mm});
            skLineSegment(sketch, "E364", {"start": v(185.64, -115.47) * mm, "end": v(186.41, -115.47) * mm});
            skLineSegment(sketch, "E365", {"start": v(162.57, -115.22) * mm, "end": v(162.57, -111.53) * mm});
            skLineSegment(sketch, "E366", {"start": v(163.83, -115.22) * mm, "end": v(163.83, -111.53) * mm});
            skLineSegment(sketch, "E367", {"start": v(182.22, -115.22) * mm, "end": v(182.22, -111.53) * mm});
            skLineSegment(sketch, "E368", {"start": v(183.49, -115.22) * mm, "end": v(183.49, -111.53) * mm});
            skLineSegment(sketch, "E369", {"start": v(172.64, -115.47) * mm, "end": v(173.42, -115.47) * mm});
            skLineSegment(sketch, "E370", {"start": v(169.47, -115.47) * mm, "end": v(170.25, -115.47) * mm});
            skLineSegment(sketch, "E371", {"start": v(177.55, -109.52) * mm, "end": v(178.33, -109.52) * mm});
            skLineSegment(sketch, "E372", {"start": v(174.38, -109.52) * mm, "end": v(175.16, -109.52) * mm});
            skLineSegment(sketch, "E373", {"start": v(157.9, -109.52) * mm, "end": v(158.68, -109.52) * mm});
            skLineSegment(sketch, "E374", {"start": v(154.73, -109.52) * mm, "end": v(155.5, -109.52) * mm});
            skLineSegment(sketch, "E375", {"start": v(149.14, -109.31) * mm, "end": v(149.68, -109.31) * mm});
            skLineSegment(sketch, "E376", {"start": v(176.14, -114.2) * mm, "end": v(176.57, -114.2) * mm});
            skLineSegment(sketch, "E377", {"start": v(171.23, -110.8) * mm, "end": v(171.66, -110.8) * mm});
            skLineSegment(sketch, "E378", {"start": v(156.49, -114.2) * mm, "end": v(156.92, -114.2) * mm});
            skLineSegment(sketch, "E379", {"start": v(155.75, -113.46) * mm, "end": v(155.75, -109.77) * mm});
            skLineSegment(sketch, "E380", {"start": v(165.74, -115.22) * mm, "end": v(165.74, -111.53) * mm});
            skLineSegment(sketch, "E381", {"start": v(172.4, -115.22) * mm, "end": v(172.4, -111.53) * mm});
            skLineSegment(sketch, "E382", {"start": v(175.4, -113.46) * mm, "end": v(175.4, -109.77) * mm});
            skLineSegment(sketch, "E383", {"start": v(185.39, -115.22) * mm, "end": v(185.39, -111.53) * mm});
            skLineSegment(sketch, "E384", {"start": v(125.48, -112.14) * mm, "end": v(125.48, -111.37) * mm});
            skLineSegment(sketch, "E385", {"start": v(125.48, -115.22) * mm, "end": v(125.48, -114.45) * mm});
            skLineSegment(sketch, "E386", {"start": v(125.48, -109.07) * mm, "end": v(125.48, -108.29) * mm});
            skLineSegment(sketch, "E387", {"start": v(122.3, -111.12) * mm, "end": v(125.23, -111.12) * mm});
            skLineSegment(sketch, "E388", {"start": v(122.3, -112.39) * mm, "end": v(125.23, -112.39) * mm});
            skLineSegment(sketch, "E389", {"start": v(122.66, -114.2) * mm, "end": v(125.23, -114.2) * mm});
            skLineSegment(sketch, "E390", {"start": v(122.66, -109.31) * mm, "end": v(125.23, -109.31) * mm});
            skLineSegment(sketch, "E391", {"start": v(125.8, -110.55) * mm, "end": v(125.8, -109.77) * mm});
            skLineSegment(sketch, "E392", {"start": v(125.8, -113.95) * mm, "end": v(125.8, -113.38) * mm});
            skLineSegment(sketch, "E393", {"start": v(128.97, -111.62) * mm, "end": v(128.97, -111.04) * mm});
            skLineSegment(sketch, "E394", {"start": v(128.97, -113.95) * mm, "end": v(128.97, -113.38) * mm});
            skLineSegment(sketch, "E395", {"start": v(132.22, -111.86) * mm, "end": v(133.63, -111.86) * mm});
            skLineSegment(sketch, "E396", {"start": v(127.3, -111.86) * mm, "end": v(128.72, -111.86) * mm});
            skLineSegment(sketch, "E397", {"start": v(132.22, -113.13) * mm, "end": v(133.63, -113.13) * mm});
            skLineSegment(sketch, "E398", {"start": v(127.3, -113.13) * mm, "end": v(128.72, -113.13) * mm});
            skLineSegment(sketch, "E399", {"start": v(127.06, -113.95) * mm, "end": v(127.06, -113.38) * mm});
            skLineSegment(sketch, "E400", {"start": v(127.3, -114.2) * mm, "end": v(128.72, -114.2) * mm});
            skLineSegment(sketch, "E401", {"start": v(126.04, -110.8) * mm, "end": v(128.72, -110.8) * mm});
            skLineSegment(sketch, "E402", {"start": v(135.15, -110.55) * mm, "end": v(135.15, -109.77) * mm});
            skLineSegment(sketch, "E403", {"start": v(135.15, -113.95) * mm, "end": v(135.15, -113.38) * mm});
            skLineSegment(sketch, "E404", {"start": v(130.7, -111.62) * mm, "end": v(130.7, -111.04) * mm});
            skLineSegment(sketch, "E405", {"start": v(130.7, -115.22) * mm, "end": v(130.7, -114.45) * mm});
            skLineSegment(sketch, "E406", {"start": v(133.88, -113.95) * mm, "end": v(133.88, -113.38) * mm});
            skLineSegment(sketch, "E407", {"start": v(131.98, -111.62) * mm, "end": v(131.98, -111.04) * mm});
            skLineSegment(sketch, "E408", {"start": v(130.95, -114.2) * mm, "end": v(133.63, -114.2) * mm});
            skLineSegment(sketch, "E409", {"start": v(132.22, -110.8) * mm, "end": v(134.9, -110.8) * mm});
            skLineSegment(sketch, "E410", {"start": v(139.27, -110.55) * mm, "end": v(139.27, -109.77) * mm});
            skLineSegment(sketch, "E411", {"start": v(139.27, -115.22) * mm, "end": v(139.27, -114.45) * mm});
            skLineSegment(sketch, "E412", {"start": v(137.38, -114.2) * mm, "end": v(139.02, -114.2) * mm});
            skLineSegment(sketch, "E413", {"start": v(137.38, -110.8) * mm, "end": v(139.02, -110.8) * mm});
            skLineSegment(sketch, "E414", {"start": v(141.34, -114.2) * mm, "end": v(142.26, -114.2) * mm});
            skLineSegment(sketch, "E415", {"start": v(141.34, -110.8) * mm, "end": v(142.26, -110.8) * mm});
            skLineSegment(sketch, "E416", {"start": v(168.75, -108.43) * mm, "end": v(168.75, -108.29) * mm});
            skLineSegment(sketch, "E417", {"start": v(168.75, -115.22) * mm, "end": v(168.75, -109.77) * mm});
            skLineSegment(sketch, "E418", {"start": v(167.48, -108.43) * mm, "end": v(167.48, -108.29) * mm});
            skLineSegment(sketch, "E419", {"start": v(167.48, -115.22) * mm, "end": v(167.48, -109.77) * mm});
            skLineSegment(sketch, "E420", {"start": v(167.73, -108.68) * mm, "end": v(168.5, -108.68) * mm});
            skLineSegment(sketch, "E421", {"start": v(152.99, -115.47) * mm, "end": v(153.76, -115.47) * mm});
            skLineSegment(sketch, "E422", {"start": v(152.99, -108.04) * mm, "end": v(153.76, -108.04) * mm});
            skLineSegment(sketch, "E423", {"start": v(148.07, -108.04) * mm, "end": v(150.75, -108.04) * mm});
            skLineSegment(sketch, "E424", {"start": v(157.9, -115.47) * mm, "end": v(158.68, -115.47) * mm});
            skLineSegment(sketch, "E425", {"start": v(167.73, -115.47) * mm, "end": v(168.5, -115.47) * mm});
            skLineSegment(sketch, "E426", {"start": v(159.64, -109.52) * mm, "end": v(160.42, -109.52) * mm});
            skLineSegment(sketch, "E427", {"start": v(167.73, -108.04) * mm, "end": v(168.5, -108.04) * mm});
            skLineSegment(sketch, "E428", {"start": v(167.73, -109.52) * mm, "end": v(168.5, -109.52) * mm});
            skLineSegment(sketch, "E429", {"start": v(169.47, -109.52) * mm, "end": v(170.25, -109.52) * mm});
            skLineSegment(sketch, "E430", {"start": v(177.55, -115.47) * mm, "end": v(178.33, -115.47) * mm});
            skLineSegment(sketch, "E431", {"start": v(179.3, -109.52) * mm, "end": v(180.07, -109.52) * mm});
            skLineSegment(sketch, "E432", {"start": v(186.66, -115.22) * mm, "end": v(186.66, -111.01) * mm});
            skLineSegment(sketch, "E433", {"start": v(179.05, -115.22) * mm, "end": v(179.05, -109.77) * mm});
            skLineSegment(sketch, "E434", {"start": v(178.57, -115.22) * mm, "end": v(178.57, -109.77) * mm});
            skLineSegment(sketch, "E435", {"start": v(174.14, -113.98) * mm, "end": v(174.14, -109.77) * mm});
            skLineSegment(sketch, "E436", {"start": v(173.66, -115.22) * mm, "end": v(173.66, -111.01) * mm});
            skLineSegment(sketch, "E437", {"start": v(169.22, -115.22) * mm, "end": v(169.22, -109.77) * mm});
            skLineSegment(sketch, "E438", {"start": v(167, -115.22) * mm, "end": v(167, -111.01) * mm});
            skLineSegment(sketch, "E439", {"start": v(159.4, -115.22) * mm, "end": v(159.4, -109.77) * mm});
            skLineSegment(sketch, "E440", {"start": v(158.92, -115.22) * mm, "end": v(158.92, -109.77) * mm});
            skLineSegment(sketch, "E441", {"start": v(154.48, -113.98) * mm, "end": v(154.48, -109.77) * mm});
            skLineSegment(sketch, "E442", {"start": v(154, -115.22) * mm, "end": v(154, -108.29) * mm});
            skLineSegment(sketch, "E443", {"start": v(152.74, -115.22) * mm, "end": v(152.74, -108.29) * mm});
            skLineSegment(sketch, "E444", {"start": v(127.3, -115.47) * mm, "end": v(129.99, -115.47) * mm});
            skLineSegment(sketch, "E445", {"start": v(122.5, -115.47) * mm, "end": v(125.23, -115.47) * mm});
            skLineSegment(sketch, "E446", {"start": v(126.04, -109.52) * mm, "end": v(128.72, -109.52) * mm});
            skLineSegment(sketch, "E447", {"start": v(122.5, -108.04) * mm, "end": v(125.23, -108.04) * mm});
            skLineSegment(sketch, "E448", {"start": v(130.95, -115.47) * mm, "end": v(133.63, -115.47) * mm});
            skLineSegment(sketch, "E449", {"start": v(132.22, -109.52) * mm, "end": v(134.9, -109.52) * mm});
            skLineSegment(sketch, "E450", {"start": v(137.21, -115.47) * mm, "end": v(139.02, -115.47) * mm});
            skLineSegment(sketch, "E451", {"start": v(137.21, -109.52) * mm, "end": v(139.02, -109.52) * mm});
            skLineSegment(sketch, "E452", {"start": v(141.17, -115.47) * mm, "end": v(142.43, -115.47) * mm});
            skLineSegment(sketch, "E453", {"start": v(141.17, -109.52) * mm, "end": v(142.43, -109.52) * mm});
            skLineSegment(sketch, "E454", {"start": v(130.23, -115.22) * mm, "end": v(130.23, -111.04) * mm});
            skLineSegment(sketch, "E455", {"start": v(53, -92.71) * mm, "end": v(53, -101.52) * mm});
            skLineSegment(sketch, "E456", {"start": v(12.84, -130.18) * mm, "end": v(12.84, -92.08) * mm});
            skLineSegment(sketch, "E457", {"start": v(108.72, -92.08) * mm, "end": v(108.72, -84.1) * mm});
            skLineSegment(sketch, "E458", {"start": v(108.72, -130.18) * mm, "end": v(108.72, -92.71) * mm});
            skLineSegment(sketch, "E459", {"start": v(186.5, -92.08) * mm, "end": v(186.5, -84.15) * mm});
            skLineSegment(sketch, "E460", {"start": v(115.07, -92.08) * mm, "end": v(115.07, -84.1) * mm});
            skLineSegment(sketch, "E461", {"start": v(192.85, -92.08) * mm, "end": v(192.85, -84.15) * mm});
            skLineSegment(sketch, "E462", {"start": v(108.72, -85.73) * mm, "end": v(205.55, -85.73) * mm});
            skLineSegment(sketch, "E463", {"start": v(108.72, -92.08) * mm, "end": v(205.55, -92.08) * mm});
            skLineSegment(sketch, "E464", {"start": v(12.84, -92.08) * mm, "end": v(111.2, -92.08) * mm});
            skLineSegment(sketch, "E465", {"start": v(108.72, -92.71) * mm, "end": v(205.55, -92.71) * mm});
            skLineSegment(sketch, "E466", {"start": v(13.47, -92.71) * mm, "end": v(108.09, -92.71) * mm});
            skLineSegment(sketch, "E467", {"start": v(108.72, -125.4) * mm, "end": v(197.62, -125.4) * mm});
            skLineSegment(sketch, "E468", {"start": v(13.47, -125.4) * mm, "end": v(108.09, -125.4) * mm});
            skLineSegment(sketch, "E469", {"start": v(108.72, -120.62) * mm, "end": v(197.62, -120.62) * mm});
            skLineSegment(sketch, "E470", {"start": v(13.47, -120.62) * mm, "end": v(108.09, -120.62) * mm});
            skLineSegment(sketch, "E471", {"start": v(13.47, -101.52) * mm, "end": v(108.09, -101.52) * mm});
            skLineSegment(sketch, "E472", {"start": v(13.47, -106.3) * mm, "end": v(108.09, -106.3) * mm});
            skLineSegment(sketch, "E473", {"start": v(13.47, -111.07) * mm, "end": v(108.09, -111.07) * mm});
            skLineSegment(sketch, "E474", {"start": v(60.78, -130.18) * mm, "end": v(60.78, -120.62) * mm});
            skLineSegment(sketch, "E475", {"start": v(13.47, -115.85) * mm, "end": v(108.09, -115.85) * mm});
            skLineSegment(sketch, "E476", {"start": v(45.22, -99.97) * mm, "end": v(45.22, -96.8) * mm});
            skLineSegment(sketch, "E477", {"start": v(42.05, -99.97) * mm, "end": v(42.05, -96.8) * mm});
            skLineSegment(sketch, "E478", {"start": v(20.64, -99.97) * mm, "end": v(20.64, -96.8) * mm});
            skLineSegment(sketch, "E479", {"start": v(23.81, -99.97) * mm, "end": v(23.81, -96.8) * mm});
            skLineSegment(sketch, "E480", {"start": v(20.64, -99.97) * mm, "end": v(23.81, -99.97) * mm});
            skLineSegment(sketch, "E481", {"start": v(42.05, -99.97) * mm, "end": v(45.22, -99.97) * mm});
            skLineSegment(sketch, "E482", {"start": v(20.64, -96.8) * mm, "end": v(23.81, -96.8) * mm});
            skLineSegment(sketch, "E483", {"start": v(42.05, -96.8) * mm, "end": v(45.22, -96.8) * mm});
            skLineSegment(sketch, "E484", {"start": v(156.35, -130.18) * mm, "end": v(156.35, -120.62) * mm});
            skLineSegment(sketch, "E485", {"start": v(155.89, -99) * mm, "end": v(187.71, -99) * mm});
            skLineSegment(sketch, "E486", {"start": v(131.44, -106.2) * mm, "end": v(151.57, -106.2) * mm});
            skLineSegment(sketch, "E487", {"start": v(197.62, -130.18) * mm, "end": v(197.62, -92.71) * mm});
            skLineSegment(sketch, "E488", {"start": v(108.09, -130.18) * mm, "end": v(108.09, -92.71) * mm});
            skLineSegment(sketch, "E489", {"start": v(13.47, -130.18) * mm, "end": v(13.47, -92.71) * mm});
            skLineSegment(sketch, "E490", {"start": v(24.45, -91.03) * mm, "end": v(23.35, -89.55) * mm});
            skLineSegment(sketch, "E491", {"start": v(23.35, -89.55) * mm, "end": v(23.35, -86.97) * mm});
            skLineSegment(sketch, "E492", {"start": v(23.35, -86.97) * mm, "end": v(24.45, -85.5) * mm});
            skLineSegment(sketch, "E493", {"start": v(27.42, -87.56) * mm, "end": v(27.42, -88.97) * mm});
            skLineSegment(sketch, "E494", {"start": v(27.42, -88.97) * mm, "end": v(28.4, -89.97) * mm});
            skLineSegment(sketch, "E495", {"start": v(28.4, -89.97) * mm, "end": v(29.81, -89.97) * mm});
            skLineSegment(sketch, "E496", {"start": v(29.81, -89.97) * mm, "end": v(30.83, -88.97) * mm});
            skLineSegment(sketch, "E497", {"start": v(30.83, -88.97) * mm, "end": v(30.83, -87.56) * mm});
            skLineSegment(sketch, "E498", {"start": v(30.83, -87.56) * mm, "end": v(29.81, -86.56) * mm});
            skLineSegment(sketch, "E499", {"start": v(29.81, -86.56) * mm, "end": v(28.4, -86.56) * mm});
            skLineSegment(sketch, "E500", {"start": v(28.4, -86.56) * mm, "end": v(27.42, -87.56) * mm});
            skLineSegment(sketch, "E501", {"start": v(26.57, -87.21) * mm, "end": v(26.57, -89.32) * mm});
            skLineSegment(sketch, "E502", {"start": v(26.57, -89.32) * mm, "end": v(28.06, -90.82) * mm});
            skLineSegment(sketch, "E503", {"start": v(28.06, -90.82) * mm, "end": v(30.18, -90.82) * mm});
            skLineSegment(sketch, "E504", {"start": v(30.18, -90.82) * mm, "end": v(31.66, -89.32) * mm});
            skLineSegment(sketch, "E505", {"start": v(31.66, -89.32) * mm, "end": v(31.66, -87.21) * mm});
            skLineSegment(sketch, "E506", {"start": v(31.66, -87.21) * mm, "end": v(30.18, -85.7) * mm});
            skLineSegment(sketch, "E507", {"start": v(30.18, -85.7) * mm, "end": v(28.06, -85.7) * mm});
            skLineSegment(sketch, "E508", {"start": v(28.06, -85.7) * mm, "end": v(26.57, -87.21) * mm});
            skLineSegment(sketch, "E509", {"start": v(33.51, -91.03) * mm, "end": v(34.61, -89.55) * mm});
            skLineSegment(sketch, "E510", {"start": v(34.61, -89.55) * mm, "end": v(34.61, -86.97) * mm});
            skLineSegment(sketch, "E511", {"start": v(34.61, -86.97) * mm, "end": v(33.51, -85.5) * mm});
            skLineSegment(sketch, "E512", {"start": v(37.58, -90.1) * mm, "end": v(37.84, -90.1) * mm});
            skLineSegment(sketch, "E513", {"start": v(37.84, -90.1) * mm, "end": v(37.84, -89.86) * mm});
            skLineSegment(sketch, "E514", {"start": v(37.84, -89.86) * mm, "end": v(37.58, -89.86) * mm});
            skLineSegment(sketch, "E515", {"start": v(37.58, -89.86) * mm, "end": v(37.58, -90.1) * mm});
            skLineSegment(sketch, "E516", {"start": v(42.83, -87.4) * mm, "end": v(42.83, -89.13) * mm});
            skLineSegment(sketch, "E517", {"start": v(42.83, -89.13) * mm, "end": v(42.05, -90.1) * mm});
            skLineSegment(sketch, "E518", {"start": v(42.05, -90.1) * mm, "end": v(41, -90.1) * mm});
            skLineSegment(sketch, "E519", {"start": v(41, -90.1) * mm, "end": v(40.2, -89.13) * mm});
            skLineSegment(sketch, "E520", {"start": v(40.2, -89.13) * mm, "end": v(40.2, -87.4) * mm});
            skLineSegment(sketch, "E521", {"start": v(40.2, -87.4) * mm, "end": v(41, -86.42) * mm});
            skLineSegment(sketch, "E522", {"start": v(41, -86.42) * mm, "end": v(42.05, -86.42) * mm});
            skLineSegment(sketch, "E523", {"start": v(42.05, -86.42) * mm, "end": v(42.83, -87.4) * mm});
            skLineSegment(sketch, "E524", {"start": v(44.68, -90.1) * mm, "end": v(45.73, -90.1) * mm});
            skLineSegment(sketch, "E525", {"start": v(44.68, -86.92) * mm, "end": v(45.2, -86.42) * mm});
            skLineSegment(sketch, "E526", {"start": v(45.2, -86.42) * mm, "end": v(45.2, -90.1) * mm});
            skLineSegment(sketch, "E527", {"start": v(50.2, -87.4) * mm, "end": v(50.2, -89.13) * mm});
            skLineSegment(sketch, "E528", {"start": v(50.2, -89.13) * mm, "end": v(49.41, -90.1) * mm});
            skLineSegment(sketch, "E529", {"start": v(49.41, -90.1) * mm, "end": v(48.36, -90.1) * mm});
            skLineSegment(sketch, "E530", {"start": v(48.36, -90.1) * mm, "end": v(47.57, -89.13) * mm});
            skLineSegment(sketch, "E531", {"start": v(47.57, -89.13) * mm, "end": v(47.57, -87.4) * mm});
            skLineSegment(sketch, "E532", {"start": v(47.57, -87.4) * mm, "end": v(48.36, -86.42) * mm});
            skLineSegment(sketch, "E533", {"start": v(48.36, -86.42) * mm, "end": v(49.41, -86.42) * mm});
            skLineSegment(sketch, "E534", {"start": v(49.41, -86.42) * mm, "end": v(50.2, -87.4) * mm});
            skLineSegment(sketch, "E535", {"start": v(57.56, -87.15) * mm, "end": v(56.78, -86.42) * mm});
            skLineSegment(sketch, "E536", {"start": v(56.78, -86.42) * mm, "end": v(54.94, -86.42) * mm});
            skLineSegment(sketch, "E537", {"start": v(54.94, -86.42) * mm, "end": v(54.94, -90.1) * mm});
            skLineSegment(sketch, "E538", {"start": v(54.94, -90.1) * mm, "end": v(56.78, -90.1) * mm});
            skLineSegment(sketch, "E539", {"start": v(56.78, -90.1) * mm, "end": v(57.56, -89.37) * mm});
            skLineSegment(sketch, "E540", {"start": v(57.56, -89.37) * mm, "end": v(57.56, -87.15) * mm});
            skLineSegment(sketch, "E541", {"start": v(61.25, -87.9) * mm, "end": v(60.73, -88.39) * mm});
            skLineSegment(sketch, "E542", {"start": v(60.73, -88.39) * mm, "end": v(58.62, -88.39) * mm});
            skLineSegment(sketch, "E543", {"start": v(58.62, -90.1) * mm, "end": v(58.62, -86.42) * mm});
            skLineSegment(sketch, "E544", {"start": v(58.62, -86.42) * mm, "end": v(60.73, -86.42) * mm});
            skLineSegment(sketch, "E545", {"start": v(60.73, -86.42) * mm, "end": v(61.25, -86.92) * mm});
            skLineSegment(sketch, "E546", {"start": v(61.25, -86.92) * mm, "end": v(61.25, -87.9) * mm});
            skLineSegment(sketch, "E547", {"start": v(63.36, -90.1) * mm, "end": v(63.62, -90.1) * mm});
            skLineSegment(sketch, "E548", {"start": v(63.62, -90.1) * mm, "end": v(63.62, -89.86) * mm});
            skLineSegment(sketch, "E549", {"start": v(63.62, -89.86) * mm, "end": v(63.36, -89.86) * mm});
            skLineSegment(sketch, "E550", {"start": v(63.36, -89.86) * mm, "end": v(63.36, -90.1) * mm});
            skLineSegment(sketch, "E551", {"start": v(72.3, -90.1) * mm, "end": v(69.67, -86.42) * mm});
            skLineSegment(sketch, "E552", {"start": v(69.67, -90.1) * mm, "end": v(72.3, -86.42) * mm});
            skLineSegment(sketch, "E553", {"start": v(79.66, -86.92) * mm, "end": v(79.66, -89.62) * mm});
            skLineSegment(sketch, "E554", {"start": v(79.66, -89.62) * mm, "end": v(79.14, -90.1) * mm});
            skLineSegment(sketch, "E555", {"start": v(79.14, -90.1) * mm, "end": v(77.82, -90.1) * mm});
            skLineSegment(sketch, "E556", {"start": v(77.82, -90.1) * mm, "end": v(77.16, -89.95) * mm});
            skLineSegment(sketch, "E557", {"start": v(79.66, -86.92) * mm, "end": v(79.14, -86.42) * mm});
            skLineSegment(sketch, "E558", {"start": v(79.14, -86.42) * mm, "end": v(77.56, -86.42) * mm});
            skLineSegment(sketch, "E559", {"start": v(77.56, -86.42) * mm, "end": v(77.03, -86.92) * mm});
            skLineSegment(sketch, "E560", {"start": v(77.03, -86.92) * mm, "end": v(77.03, -87.9) * mm});
            skLineSegment(sketch, "E561", {"start": v(77.03, -87.9) * mm, "end": v(77.56, -88.39) * mm});
            skLineSegment(sketch, "E562", {"start": v(77.56, -88.39) * mm, "end": v(79.14, -88.39) * mm});
            skLineSegment(sketch, "E563", {"start": v(79.14, -88.39) * mm, "end": v(79.66, -87.9) * mm});
            skLineSegment(sketch, "E564", {"start": v(83.35, -87.4) * mm, "end": v(83.35, -89.13) * mm});
            skLineSegment(sketch, "E565", {"start": v(83.35, -89.13) * mm, "end": v(82.56, -90.1) * mm});
            skLineSegment(sketch, "E566", {"start": v(82.56, -90.1) * mm, "end": v(81.5, -90.1) * mm});
            skLineSegment(sketch, "E567", {"start": v(81.5, -90.1) * mm, "end": v(80.72, -89.13) * mm});
            skLineSegment(sketch, "E568", {"start": v(80.72, -89.13) * mm, "end": v(80.72, -87.4) * mm});
            skLineSegment(sketch, "E569", {"start": v(80.72, -87.4) * mm, "end": v(81.5, -86.42) * mm});
            skLineSegment(sketch, "E570", {"start": v(81.5, -86.42) * mm, "end": v(82.56, -86.42) * mm});
            skLineSegment(sketch, "E571", {"start": v(82.56, -86.42) * mm, "end": v(83.35, -87.4) * mm});
            skLineSegment(sketch, "E572", {"start": v(84.84, -87.04) * mm, "end": v(85.02, -87.47) * mm});
            skLineSegment(sketch, "E573", {"start": v(85.02, -87.47) * mm, "end": v(85.45, -87.65) * mm});
            skLineSegment(sketch, "E574", {"start": v(85.45, -87.65) * mm, "end": v(85.89, -87.47) * mm});
            skLineSegment(sketch, "E575", {"start": v(85.89, -87.47) * mm, "end": v(86.07, -87.04) * mm});
            skLineSegment(sketch, "E576", {"start": v(86.07, -87.04) * mm, "end": v(85.89, -86.6) * mm});
            skLineSegment(sketch, "E577", {"start": v(85.89, -86.6) * mm, "end": v(85.45, -86.42) * mm});
            skLineSegment(sketch, "E578", {"start": v(85.45, -86.42) * mm, "end": v(85.02, -86.6) * mm});
            skLineSegment(sketch, "E579", {"start": v(85.02, -86.6) * mm, "end": v(84.84, -87.04) * mm});
            skLineSegment(sketch, "E580", {"start": v(88.87, -86.42) * mm, "end": v(89.93, -86.42) * mm});
            skLineSegment(sketch, "E581", {"start": v(89.4, -90.1) * mm, "end": v(89.4, -86.42) * mm});
            skLineSegment(sketch, "E582", {"start": v(88.87, -90.1) * mm, "end": v(89.93, -90.1) * mm});
            skLineSegment(sketch, "E583", {"start": v(92.82, -90.1) * mm, "end": v(93.08, -90.1) * mm});
            skLineSegment(sketch, "E584", {"start": v(93.08, -90.1) * mm, "end": v(93.08, -89.86) * mm});
            skLineSegment(sketch, "E585", {"start": v(93.08, -89.86) * mm, "end": v(92.82, -89.86) * mm});
            skLineSegment(sketch, "E586", {"start": v(92.82, -89.86) * mm, "end": v(92.82, -90.1) * mm});
            skLineSegment(sketch, "E587", {"start": v(98.08, -87.15) * mm, "end": v(97.3, -86.42) * mm});
            skLineSegment(sketch, "E588", {"start": v(97.3, -86.42) * mm, "end": v(95.45, -86.42) * mm});
            skLineSegment(sketch, "E589", {"start": v(95.45, -86.42) * mm, "end": v(95.45, -90.1) * mm});
            skLineSegment(sketch, "E590", {"start": v(95.45, -90.1) * mm, "end": v(97.3, -90.1) * mm});
            skLineSegment(sketch, "E591", {"start": v(97.3, -90.1) * mm, "end": v(98.08, -89.37) * mm});
            skLineSegment(sketch, "E592", {"start": v(98.08, -89.37) * mm, "end": v(98.08, -87.15) * mm});
            skLineSegment(sketch, "E593", {"start": v(100.19, -90.1) * mm, "end": v(100.45, -90.1) * mm});
            skLineSegment(sketch, "E594", {"start": v(100.45, -90.1) * mm, "end": v(100.45, -89.86) * mm});
            skLineSegment(sketch, "E595", {"start": v(100.45, -89.86) * mm, "end": v(100.19, -89.86) * mm});
            skLineSegment(sketch, "E596", {"start": v(100.19, -89.86) * mm, "end": v(100.19, -90.1) * mm});
            skLineSegment(sketch, "E597", {"start": v(23.16, -99.97) * mm, "end": v(23.81, -99.32) * mm});
            skLineSegment(sketch, "E598", {"start": v(23.81, -98.06) * mm, "end": v(21.9, -99.97) * mm});
            skLineSegment(sketch, "E599", {"start": v(20.64, -99.97) * mm, "end": v(23.81, -96.8) * mm});
            skLineSegment(sketch, "E600", {"start": v(22.56, -96.8) * mm, "end": v(20.64, -98.72) * mm});
            skLineSegment(sketch, "E601", {"start": v(20.64, -97.46) * mm, "end": v(21.3, -96.8) * mm});
            skArc(sketch, "E602", {"start": v(59.52, 45.12) * mm, "mid": v(59.4, 45.39) * mm, "end": v(59.14, 45.5) * mm});
            skArc(sketch, "E603", {"start": v(59.14, 48.67) * mm, "mid": v(59.4, 48.79) * mm, "end": v(59.52, 49.06) * mm});
            skArc(sketch, "E604", {"start": v(62.7, 62.03) * mm, "mid": v(62, 64) * mm, "end": v(60.24, 65.12) * mm});
            skLineSegment(sketch, "E605", {"start": v(59.52, 60.25) * mm, "end": v(59.52, 61.98) * mm});
            skArc(sketch, "E606", {"start": v(59.52, 59.44) * mm, "mid": v(59.37, 59.84) * mm, "end": v(59, 60.03) * mm});
            skLineSegment(sketch, "E607", {"start": v(47.35, 61.1) * mm, "end": v(59, 60.03) * mm});
            skArc(sketch, "E608", {"start": v(59.14, 62.26) * mm, "mid": v(59.4, 62.38) * mm, "end": v(59.52, 62.64) * mm});
            skArc(sketch, "E609", {"start": v(50, 46.08) * mm, "mid": v(50.17, 45.67) * mm, "end": v(50.58, 45.5) * mm});
            skArc(sketch, "E610", {"start": v(50.58, 48.67) * mm, "mid": v(50.17, 48.5) * mm, "end": v(50, 48.1) * mm});
            skArc(sketch, "E611", {"start": v(47.4, 62.26) * mm, "mid": v(46.82, 61.7) * mm, "end": v(47.35, 61.1) * mm});
            skArc(sketch, "E612", {"start": v(60.24, 65.12) * mm, "mid": v(59.74, 65) * mm, "end": v(59.52, 64.55) * mm});
            skLineSegment(sketch, "E613", {"start": v(59.52, 62.64) * mm, "end": v(59.52, 64.55) * mm});
            skLineSegment(sketch, "E614", {"start": v(59.52, 49.06) * mm, "end": v(59.52, 59.44) * mm});
            skArc(sketch, "E615", {"start": v(-109.34, 45.5) * mm, "mid": v(-108.93, 45.67) * mm, "end": v(-108.75, 46.08) * mm});
            skArc(sketch, "E616", {"start": v(-108.75, 48.1) * mm, "mid": v(-108.93, 48.5) * mm, "end": v(-109.34, 48.67) * mm});
            skArc(sketch, "E617", {"start": v(-118.28, 49.06) * mm, "mid": v(-118.17, 48.79) * mm, "end": v(-117.9, 48.67) * mm});
            skArc(sketch, "E618", {"start": v(-118.28, 39.15) * mm, "mid": v(-118.17, 38.88) * mm, "end": v(-117.9, 38.77) * mm});
            skArc(sketch, "E619", {"start": v(-117.9, 45.5) * mm, "mid": v(-118.17, 45.39) * mm, "end": v(-118.28, 45.12) * mm});
            skArc(sketch, "E620", {"start": v(-118.28, 65.13) * mm, "mid": v(-120.52, 64.2) * mm, "end": v(-121.45, 61.96) * mm});
            skArc(sketch, "E621", {"start": v(-117.75, 60.03) * mm, "mid": v(-118.13, 59.84) * mm, "end": v(-118.28, 59.44) * mm});
            skLineSegment(sketch, "E622", {"start": v(-106.1, 61.1) * mm, "end": v(-117.75, 60.03) * mm});
            skArc(sketch, "E623", {"start": v(-118.28, 63.06) * mm, "mid": v(-118.04, 62.5) * mm, "end": v(-117.48, 62.26) * mm});
            skArc(sketch, "E624", {"start": v(-117.48, 63.86) * mm, "mid": v(-118.04, 63.63) * mm, "end": v(-118.28, 63.06) * mm});
            skArc(sketch, "E625", {"start": v(-114.14, 63.86) * mm, "mid": v(-113.69, 64.05) * mm, "end": v(-113.5, 64.5) * mm});
            skArc(sketch, "E626", {"start": v(-113.5, 64.5) * mm, "mid": v(-113.69, 64.95) * mm, "end": v(-114.14, 65.13) * mm});
            skArc(sketch, "E627", {"start": v(-106.1, 61.1) * mm, "mid": v(-105.58, 61.7) * mm, "end": v(-106.16, 62.26) * mm});
            skLineSegment(sketch, "E628", {"start": v(-118.28, 60.3) * mm, "end": v(-118.28, 62.08) * mm});
            skLineSegment(sketch, "E629", {"start": v(-118.28, 49.06) * mm, "end": v(-118.28, 59.44) * mm});
            skLineSegment(sketch, "E630", {"start": v(-117.48, 63.86) * mm, "end": v(-114.14, 63.86) * mm});
            skLineSegment(sketch, "E631", {"start": v(47.4, 62.26) * mm, "end": v(59.14, 62.26) * mm});
            skLineSegment(sketch, "E632", {"start": v(-117.48, 62.26) * mm, "end": v(-106.16, 62.26) * mm});
            skLineSegment(sketch, "E633", {"start": v(-108.75, 46.08) * mm, "end": v(-108.75, 48.1) * mm});
            skLineSegment(sketch, "E634", {"start": v(-118.28, 39.15) * mm, "end": v(-118.28, 45.12) * mm});
            skLineSegment(sketch, "E635", {"start": v(59.52, 39.15) * mm, "end": v(59.52, 45.12) * mm});
            skLineSegment(sketch, "E636", {"start": v(50, 46.08) * mm, "end": v(50, 48.1) * mm});
            skLineSegment(sketch, "E637", {"start": v(-117.9, 45.5) * mm, "end": v(-109.34, 45.5) * mm});
            skLineSegment(sketch, "E638", {"start": v(-117.9, 48.67) * mm, "end": v(-109.34, 48.67) * mm});
            skLineSegment(sketch, "E639", {"start": v(59.14, 45.5) * mm, "end": v(50.58, 45.5) * mm});
            skLineSegment(sketch, "E640", {"start": v(59.14, 48.67) * mm, "end": v(50.58, 48.67) * mm});
            skLineSegment(sketch, "E641", {"start": v(-118.28, 65.13) * mm, "end": v(-114.14, 65.13) * mm});
            skLineSegment(sketch, "E642", {"start": v(-117.9, 38.77) * mm, "end": v(-109.13, 38.77) * mm});
            skLineSegment(sketch, "E643", {"start": v(62.7, 38.77) * mm, "end": v(62.7, 62.03) * mm});
            skLineSegment(sketch, "E644", {"start": v(-121.45, 38.77) * mm, "end": v(-121.45, 61.96) * mm});
            skSolve(sketch);
        }
        {
            var Q0;
            Q0=makeQuery(id+"F0.imprint","IMPRINT",FACE,{"disambiguationData":[TD([[makeQuery(id+"F0.imprint","IMPRINT",EDGE,{"derivedFrom":sQuery(id+"F0.wireOp",EDGE,"E5")}),1.0]])]});
            extrude(context, id + "F1", {"entities" : qUnion([Q0]), "depth" : 508 * mm, "offsetDistance" : 25.4 * mm});
        }
    });
